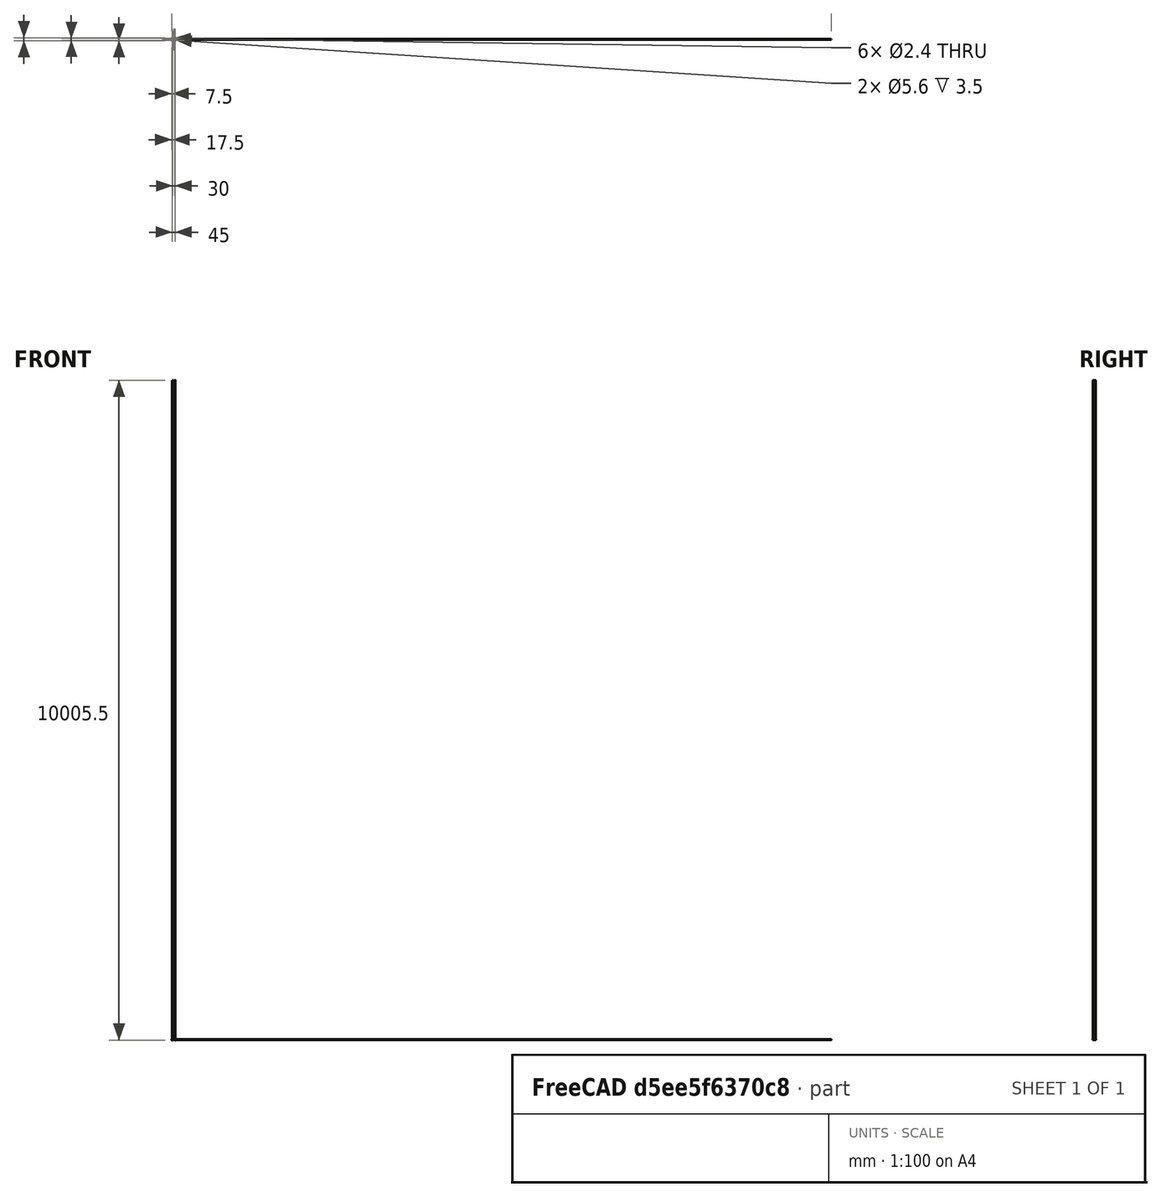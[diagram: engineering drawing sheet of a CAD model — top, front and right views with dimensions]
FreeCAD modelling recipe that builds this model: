
FCSTD DOCUMENT  (FreeCAD 0.16R)
Label: 60mmPed2
License: All rights reserved
LicenseURL: http://en.wikipedia.org/wiki/All_rights_reserved
objects: Sketcher::SketchObject×8, PartDesign::Pocket×6, PartDesign::Chamfer×4, PartDesign::Pad×2, PartDesign::Fillet×1, Mesh::Feature×1
note: 29 computed .brp shape members not serialized (recipe doc carries the construction recipe); baked Part::Feature solids carry a one-line shape summary decoded from their .brp

FEATURE [Sketcher::SketchObject] Sketch
  sketch-geometry (8):
    g0: LineSegment StartX=25 StartY=-12.5 StartZ=0 EndX=25 EndY=12.5 EndZ=0
    g1: LineSegment StartX=15 StartY=22.5 StartZ=0 EndX=-15 EndY=22.5 EndZ=0
    g2: LineSegment StartX=15 StartY=-22.5 StartZ=0 EndX=-15 EndY=-22.5 EndZ=0
    g3: LineSegment StartX=-32.5 StartY=5 StartZ=0 EndX=-32.5 EndY=-5 EndZ=0
    g4: ArcOfCircle CenterX=-15 CenterY=5 CenterZ=0 NormalX=0 NormalY=0 NormalZ=1 Radius=17.5 StartAngle=1.5708 EndAngle=3.14159
    g5: ArcOfCircle CenterX=-15 CenterY=-5 CenterZ=0 NormalX=0 NormalY=0 NormalZ=1 Radius=17.5 StartAngle=3.14159 EndAngle=4.71239
    g6: ArcOfCircle CenterX=15 CenterY=-12.5 CenterZ=0 NormalX=0 NormalY=0 NormalZ=1 Radius=10 StartAngle=4.71239 EndAngle=6.28319
    g7: ArcOfCircle CenterX=15 CenterY=12.5 CenterZ=0 NormalX=0 NormalY=0 NormalZ=1 Radius=10 StartAngle=0 EndAngle=1.5708
  constraints (20):
    c: Horizontal(g1)
    c: Horizontal(g2)
    c: Equal(g2,g1)
    c: Tangent(g3,g4) = -1.5708
    c: Tangent(g1,g4) = -1.5708
    c: Tangent(g3,g5) = -1.5708
    c: Tangent(g2,g5) = 1.5708
    c: Tangent(g2,g6) = 1.5708
    c: Tangent(g0,g6) = -1.5708
    c: Tangent(g1,g7) = -1.5708
    c: Tangent(g0,g7) = -1.5708
    c: Vertical(g3)
    c: Vertical(g0)
    c: Symmetric(g3,g3,g-1)
    c: Symmetric(g0,g0,g-1)
    c: Symmetric(g1,g1,g-2)
    c: Distance(g0,g3) = 57.5
    c: Distance(g1,g2) = 45
    c: Distance(g3) = 10
    c: Distance(g0) = 25
FEATURE [PartDesign::Pad] Pad
  Length = 7
  Length2 = 100
  Sketch = -> Sketch
  Type = 0
FEATURE [Sketcher::SketchObject] Sketch003
  Placement = pos=(-32.5,0,0) rot=(0.57735,-0.57735,-0.57735;2.0944rad)
  Support = -> Pad [Face6]
  sketch-geometry (1):
    g0: Circle CenterX=0 CenterY=0 CenterZ=0 NormalX=0 NormalY=0 NormalZ=1 Radius=5.5
  constraints (2):
    c: Coincident(g0,g-1)
    c: Radius(g0) = 5.5
FEATURE [PartDesign::Pocket] Pocket
  Length = 8
  Sketch = -> Sketch003
  Type = 0
FEATURE [Sketcher::SketchObject] Sketch001
  Placement = pos=(25,0,0) rot=(0.57735,0.57735,0.57735;2.0944rad)
  Support = -> Pocket [Face3]
  sketch-geometry (1):
    g0: Circle CenterX=0 CenterY=0 CenterZ=0 NormalX=0 NormalY=0 NormalZ=1 Radius=5.5
  constraints (2):
    c: Coincident(g0,g-1)
    c: Radius(g0) = 5.5
FEATURE [PartDesign::Pocket] Pocket001
  Length = 8
  Sketch = -> Sketch001
  Type = 0
FEATURE [Sketcher::SketchObject] Sketch002
  Placement = pos=(-32.5,0,0) rot=(0.57735,-0.57735,-0.57735;2.0944rad)
  Support = -> Pocket001 [Face14]
  sketch-geometry (1):
    g0: Circle CenterX=0 CenterY=0 CenterZ=0 NormalX=0 NormalY=0 NormalZ=1 Radius=4.25
  constraints (2):
    c: Radius(g0) = 4.25
    c: Coincident(g0,g-1)
FEATURE [PartDesign::Pocket] Pocket002
  Length = 5
  Sketch = -> Sketch002
  Type = 1
FEATURE [Sketcher::SketchObject] Sketch005
  Placement = pos=(0,0,0) rot=(1,0,0;3.14159rad)
  Support = -> Pocket002 [Face8]
  sketch-geometry (2):
    g0: Circle CenterX=15 CenterY=-15 CenterZ=0 NormalX=0 NormalY=0 NormalZ=1 Radius=2.75
    g1: Circle CenterX=-15 CenterY=-15 CenterZ=0 NormalX=0 NormalY=0 NormalZ=1 Radius=2.75
  constraints (5):
    c: Radius(g1) = 2.75
    c: Equal(g1,g0)
    c: Symmetric(g0,g1,g-2)
    c: Distance(g0,g1) = 30
    c: DistanceY(g0) = -15
FEATURE [PartDesign::Pad] Pad001
  Length = 1
  Length2 = 100
  Sketch = -> Sketch005
  Type = 0
FEATURE [Sketcher::SketchObject] Sketch004
  Placement = pos=(0,0,0) rot=(1,0,0;3.14159rad)
  Support = -> Pad001 [Face4]
  sketch-geometry (2):
    g0: Circle CenterX=15 CenterY=15 CenterZ=0 NormalX=0 NormalY=0 NormalZ=1 Radius=2.8
    g1: Circle CenterX=-15 CenterY=15 CenterZ=0 NormalX=0 NormalY=0 NormalZ=1 Radius=2.8
  constraints (5):
    c: Radius(g0) = 2.8
    c: Equal(g0,g1)
    c: Symmetric(g1,g0,g-2)
    c: Distance(g0,g1) = 30
    c: DistanceY(g0) = 15
FEATURE [PartDesign::Pocket] Pocket003
  Length = 4
  Sketch = -> Sketch004
  Type = 0
FEATURE [Sketcher::SketchObject] Sketch006
  Placement = pos=(0,0,0) rot=(1,0,0;3.14159rad)
  Support = -> Pocket003 [Face4]
  sketch-geometry (6):
    g0: Circle CenterX=-25 CenterY=10 CenterZ=0 NormalX=0 NormalY=0 NormalZ=1 Radius=1.2
    g1: Circle CenterX=0 CenterY=-15 CenterZ=0 NormalX=0 NormalY=0 NormalZ=1 Radius=1.2
    g2: Circle CenterX=0 CenterY=15 CenterZ=0 NormalX=0 NormalY=0 NormalZ=1 Radius=1.2
    g3: Circle CenterX=-25 CenterY=-10 CenterZ=0 NormalX=0 NormalY=0 NormalZ=1 Radius=1.2
    g4: Circle CenterX=20 CenterY=10 CenterZ=0 NormalX=0 NormalY=0 NormalZ=1 Radius=1.2
    g5: Circle CenterX=20 CenterY=-10 CenterZ=0 NormalX=0 NormalY=0 NormalZ=1 Radius=1.2
  constraints (16):
    c: Radius(g1) = 1.2
    c: Equal(g1,g0)
    c: Equal(g1,g2)
    c: Equal(g1,g3)
    c: Equal(g1,g5)
    c: Equal(g1,g4)
    c: PointOnObject(g1,g-2)
    c: PointOnObject(g2,g-2)
    c: Symmetric(g5,g4,g-1)
    c: Symmetric(g3,g0,g-1)
    c: Distance(g0,g3) = 20
    c: Distance(g4,g5) = 20
    c: DistanceX(g4) = 20
    c: DistanceX(g0) = -25
    c: Symmetric(g1,g2,g-1)
    c: Distance(g1,g2) = 30
FEATURE [PartDesign::Pocket] Pocket004
  Length = 5
  Sketch = -> Sketch006
  Type = 1
FEATURE [Sketcher::SketchObject] Sketch007
  ExternalGeometry = -> [Pocket004]
  Placement = pos=(0,0,7) rot=(0,0,1;0rad)
  Support = -> Pocket004 [Face5]
  sketch-geometry (42):
    g0: LineSegment StartX=-25 StartY=7.57513 StartZ=0 EndX=-22.9 EndY=8.78756 EndZ=0
    g1: LineSegment StartX=-22.9 StartY=8.78756 StartZ=0 EndX=-22.9 EndY=11.2124 EndZ=0
    g2: LineSegment StartX=-22.9 StartY=11.2124 StartZ=0 EndX=-25 EndY=12.4249 EndZ=0
    g3: LineSegment StartX=-25 StartY=12.4249 StartZ=0 EndX=-27.1 EndY=11.2124 EndZ=0
    g4: LineSegment StartX=-27.1 StartY=11.2124 StartZ=0 EndX=-27.1 EndY=8.78757 EndZ=0
    g5: LineSegment StartX=-27.1 StartY=8.78757 StartZ=0 EndX=-25 EndY=7.57513 EndZ=0
    g6: Circle [constr] CenterX=-25 CenterY=10 CenterZ=0 NormalX=0 NormalY=0 NormalZ=1 Radius=2.42487
    g7: LineSegment StartX=-3.46023e-07 StartY=-17.4249 StartZ=0 EndX=2.1 EndY=-16.2124 EndZ=0
    g8: LineSegment StartX=2.1 StartY=-16.2124 StartZ=0 EndX=2.1 EndY=-13.7876 EndZ=0
    g9: LineSegment StartX=2.1 StartY=-13.7876 StartZ=0 EndX=-2.325e-08 EndY=-12.5751 EndZ=0
    g10: LineSegment StartX=-2.325e-08 StartY=-12.5751 StartZ=0 EndX=-2.1 EndY=-13.7876 EndZ=0
    g11: LineSegment StartX=-2.1 StartY=-13.7876 StartZ=0 EndX=-2.1 EndY=-16.2124 EndZ=0
    g12: LineSegment StartX=-2.1 StartY=-16.2124 StartZ=0 EndX=-3.46023e-07 EndY=-17.4249 EndZ=0
    g13: Circle [constr] CenterX=3.255e-09 CenterY=-15 CenterZ=0 NormalX=0 NormalY=0 NormalZ=1 Radius=2.42487
    g14: LineSegment StartX=-25 StartY=-12.4249 StartZ=0 EndX=-22.9 EndY=-11.2124 EndZ=0
    g15: LineSegment StartX=-22.9 StartY=-11.2124 StartZ=0 EndX=-22.9 EndY=-8.78757 EndZ=0
    g16: LineSegment StartX=-22.9 StartY=-8.78757 StartZ=0 EndX=-25 EndY=-7.57513 EndZ=0
    g17: LineSegment StartX=-25 StartY=-7.57513 StartZ=0 EndX=-27.1 EndY=-8.78757 EndZ=0
    g18: LineSegment StartX=-27.1 StartY=-8.78757 StartZ=0 EndX=-27.1 EndY=-11.2124 EndZ=0
    g19: LineSegment StartX=-27.1 StartY=-11.2124 StartZ=0 EndX=-25 EndY=-12.4249 EndZ=0
    g20: Circle [constr] CenterX=-25 CenterY=-10 CenterZ=0 NormalX=0 NormalY=0 NormalZ=1 Radius=2.42487
    g21: LineSegment StartX=-1.23206e-06 StartY=12.5751 StartZ=0 EndX=2.1 EndY=13.7876 EndZ=0
    g22: LineSegment StartX=2.1 StartY=13.7876 StartZ=0 EndX=2.1 EndY=16.2124 EndZ=0
    g23: LineSegment StartX=2.1 StartY=16.2124 StartZ=0 EndX=-8.17872e-07 EndY=17.4249 EndZ=0
    g24: LineSegment StartX=-8.17872e-07 StartY=17.4249 StartZ=0 EndX=-2.1 EndY=16.2124 EndZ=0
    g25: LineSegment StartX=-2.1 StartY=16.2124 StartZ=0 EndX=-2.1 EndY=13.7876 EndZ=0
    g26: LineSegment StartX=-2.1 StartY=13.7876 StartZ=0 EndX=-1.23206e-06 EndY=12.5751 EndZ=0
    g27: Circle [constr] CenterX=-5.1841e-08 CenterY=15 CenterZ=0 NormalX=0 NormalY=0 NormalZ=1 Radius=2.42487
    g28: LineSegment StartX=20 StartY=-12.4249 StartZ=0 EndX=22.1 EndY=-11.2124 EndZ=0
    g29: LineSegment StartX=22.1 StartY=-11.2124 StartZ=0 EndX=22.1 EndY=-8.78756 EndZ=0
    g30: LineSegment StartX=22.1 StartY=-8.78756 StartZ=0 EndX=20 EndY=-7.57513 EndZ=0
    g31: LineSegment StartX=20 StartY=-7.57513 StartZ=0 EndX=17.9 EndY=-8.78756 EndZ=0
    g32: LineSegment StartX=17.9 StartY=-8.78756 StartZ=0 EndX=17.9 EndY=-11.2124 EndZ=0
    g33: LineSegment StartX=17.9 StartY=-11.2124 StartZ=0 EndX=20 EndY=-12.4249 EndZ=0
    g34: Circle [constr] CenterX=20 CenterY=-10 CenterZ=0 NormalX=0 NormalY=0 NormalZ=1 Radius=2.42487
    g35: LineSegment StartX=20 StartY=7.57513 StartZ=0 EndX=22.1 EndY=8.78757 EndZ=0
    g36: LineSegment StartX=22.1 StartY=8.78757 StartZ=0 EndX=22.1 EndY=11.2124 EndZ=0
    g37: LineSegment StartX=22.1 StartY=11.2124 StartZ=0 EndX=20 EndY=12.4249 EndZ=0
    g38: LineSegment StartX=20 StartY=12.4249 StartZ=0 EndX=17.9 EndY=11.2124 EndZ=0
    g39: LineSegment StartX=17.9 StartY=11.2124 StartZ=0 EndX=17.9 EndY=8.78756 EndZ=0
    g40: LineSegment StartX=17.9 StartY=8.78756 StartZ=0 EndX=20 EndY=7.57513 EndZ=0
    g41: Circle [constr] CenterX=20 CenterY=10 CenterZ=0 NormalX=0 NormalY=0 NormalZ=1 Radius=2.42487
  constraints (96):
    c: Coincident(g0,g1)
    c: Coincident(g1,g2)
    c: Coincident(g2,g3)
    c: Coincident(g3,g4)
    c: Coincident(g4,g5)
    c: Coincident(g5,g0)
    c: Equal(g0, g1-g5) x5
    c: PointOnObject(g0,g6)
    c: PointOnObject(g1,g6)
    c: PointOnObject(g2,g6)
    c: PointOnObject(g3,g6)
    c: PointOnObject(g4,g6)
    c: PointOnObject(g5,g6)
    c: Distance(g0,g3) = 4.2
    c: Coincident(g-3,g6)
    c: Coincident(g7,g8)
    c: Coincident(g8,g9)
    c: Coincident(g9,g10)
    c: Coincident(g10,g11)
    c: Coincident(g11,g12)
    c: Coincident(g12,g7)
    c: Equal(g7, g8-g12) x5
    c: PointOnObject(g7,g13)
    c: PointOnObject(g8,g13)
    c: PointOnObject(g9,g13)
    c: PointOnObject(g10,g13)
    c: PointOnObject(g11,g13)
    c: PointOnObject(g12,g13)
    c: Coincident(g14,g15)
    c: Coincident(g15,g16)
    c: Coincident(g16,g17)
    c: Coincident(g17,g18)
    c: Coincident(g18,g19)
    c: Coincident(g19,g14)
    c: Equal(g14, g15-g19) x5
    c: PointOnObject(g14,g20)
    c: PointOnObject(g15,g20)
    c: PointOnObject(g16,g20)
    c: PointOnObject(g17,g20)
    c: PointOnObject(g18,g20)
    c: PointOnObject(g19,g20)
    c: Coincident(g21,g22)
    c: Coincident(g22,g23)
    c: Coincident(g23,g24)
    c: Coincident(g24,g25)
    c: Coincident(g25,g26)
    c: Coincident(g26,g21)
    c: Equal(g21, g22-g26) x5
    c: PointOnObject(g21,g27)
    c: PointOnObject(g22,g27)
    c: PointOnObject(g23,g27)
    c: PointOnObject(g24,g27)
    c: PointOnObject(g25,g27)
    c: PointOnObject(g26,g27)
    c: Distance(g21,g24) = 4.2
    c: Distance(g14,g17) = 4.2
    c: Distance(g7,g10) = 4.2
    c: Coincident(g13,g-4)
    c: Coincident(g20,g-6)
    c: Coincident(g27,g-7)
    c: Coincident(g28,g29)
    c: Coincident(g29,g30)
    c: Coincident(g30,g31)
    c: Coincident(g31,g32)
    c: Coincident(g32,g33)
    c: Coincident(g33,g28)
    c: Equal(g28, g29-g33) x5
    c: PointOnObject(g28,g34)
    c: PointOnObject(g29,g34)
    c: PointOnObject(g30,g34)
    c: PointOnObject(g31,g34)
    c: PointOnObject(g32,g34)
    c: PointOnObject(g33,g34)
    c: Coincident(g35,g36)
    c: Coincident(g36,g37)
    c: Coincident(g37,g38)
    c: Coincident(g38,g39)
    c: Coincident(g39,g40)
    c: Coincident(g40,g35)
    c: Equal(g35, g36-g40) x5
    c: PointOnObject(g35,g41)
    c: PointOnObject(g36,g41)
    c: PointOnObject(g37,g41)
    c: PointOnObject(g38,g41)
    c: PointOnObject(g39,g41)
    c: PointOnObject(g40,g41)
    c: Distance(g35,g37) = 4.2
    c: Distance(g28,g30) = 4.2
    c: Coincident(g34,g-8)
    c: Coincident(g41,g-5)
    c: Vertical(g1)
    c: Vertical(g22)
    c: Vertical(g8)
    c: Vertical(g29)
    c: Vertical(g36)
    c: Vertical(g15)
FEATURE [PartDesign::Pocket] Pocket005
  Length = 2
  Sketch = -> Sketch007
  Type = 0
FEATURE [PartDesign::Chamfer] Chamfer
  Base = -> Pocket005 [Edge178,Edge176]
  Size = 0.5
FEATURE [PartDesign::Chamfer] Chamfer001
  Base = -> Chamfer [Edge57,Edge55]
  Size = 0.5
FEATURE [PartDesign::Fillet] Fillet
  Base = -> Chamfer001 [Edge35,Edge38]
  Radius = 1
FEATURE [PartDesign::Chamfer] Chamfer002
  Base = -> Fillet [Edge67]
  Size = 0.69
FEATURE [PartDesign::Chamfer] Chamfer003
  Base = -> Chamfer002 [Edge206,Edge97,Edge198,Edge200,Edge101,Edge99]
  Size = 0.75
FEATURE [Mesh::Feature] Mesh  label="Chamfer003 (Meshed)"
